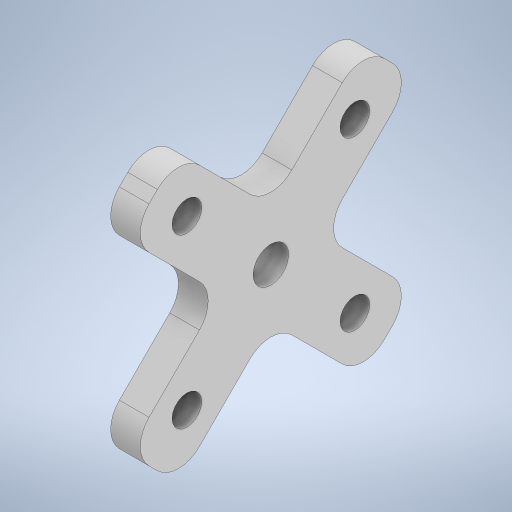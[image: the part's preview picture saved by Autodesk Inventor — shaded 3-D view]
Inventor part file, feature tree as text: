
AUTODESK INVENTOR PART (.ipt)
format: ipt  version: 2023 (Build 270158000, 158)  size: 665,600 bytes
history: native  units: in
note: dims shown in document units (in); Inventor stores cm internally (conversion verified against a paired STEP export)
features: extrude x3, fillet x3, sketch x3
ambient origin geometry x8: Origin, YZ Plane, XZ Plane, XY Plane, X Axis, Y Axis, Z Axis, Center Point
bodies: Solid1 (feature_tree)
feature tree (9):
  extrude  "Extrusion1"  Depth=1.414in
  fillet  "Fillet1"  Radius=0.3in
  extrude  "Extrusion2"  Depth=0.25in
  extrude  "Extrusion3"  Depth=0.25in
  fillet  "Fillet2"  Radius=0.3in
  fillet  "Fillet3"  Radius=1.4in
  sketch  "Sketch1"  dims[d0=1.414in d1=1.414in d2=0.3in]
  sketch  "Sketch2"  dims[d3=0.25in d4=0.25in]
  sketch  "Sketch3"  dims[d5=0.25in d6=0.25in d7=0.3in d8=1.4in d9=0.6in d10=1.4in d11=0.6in d12=1.4in d13=0.25in d14=0.0in d15=0.25in d16=0.25in d17=0.25in d18=0.0in d19=0.0in d20=0.24in d21=0.24in d22=0.24in d23=0.24in d24=0.5in d25=0.0in d26=0.03in d27=0.05in]
